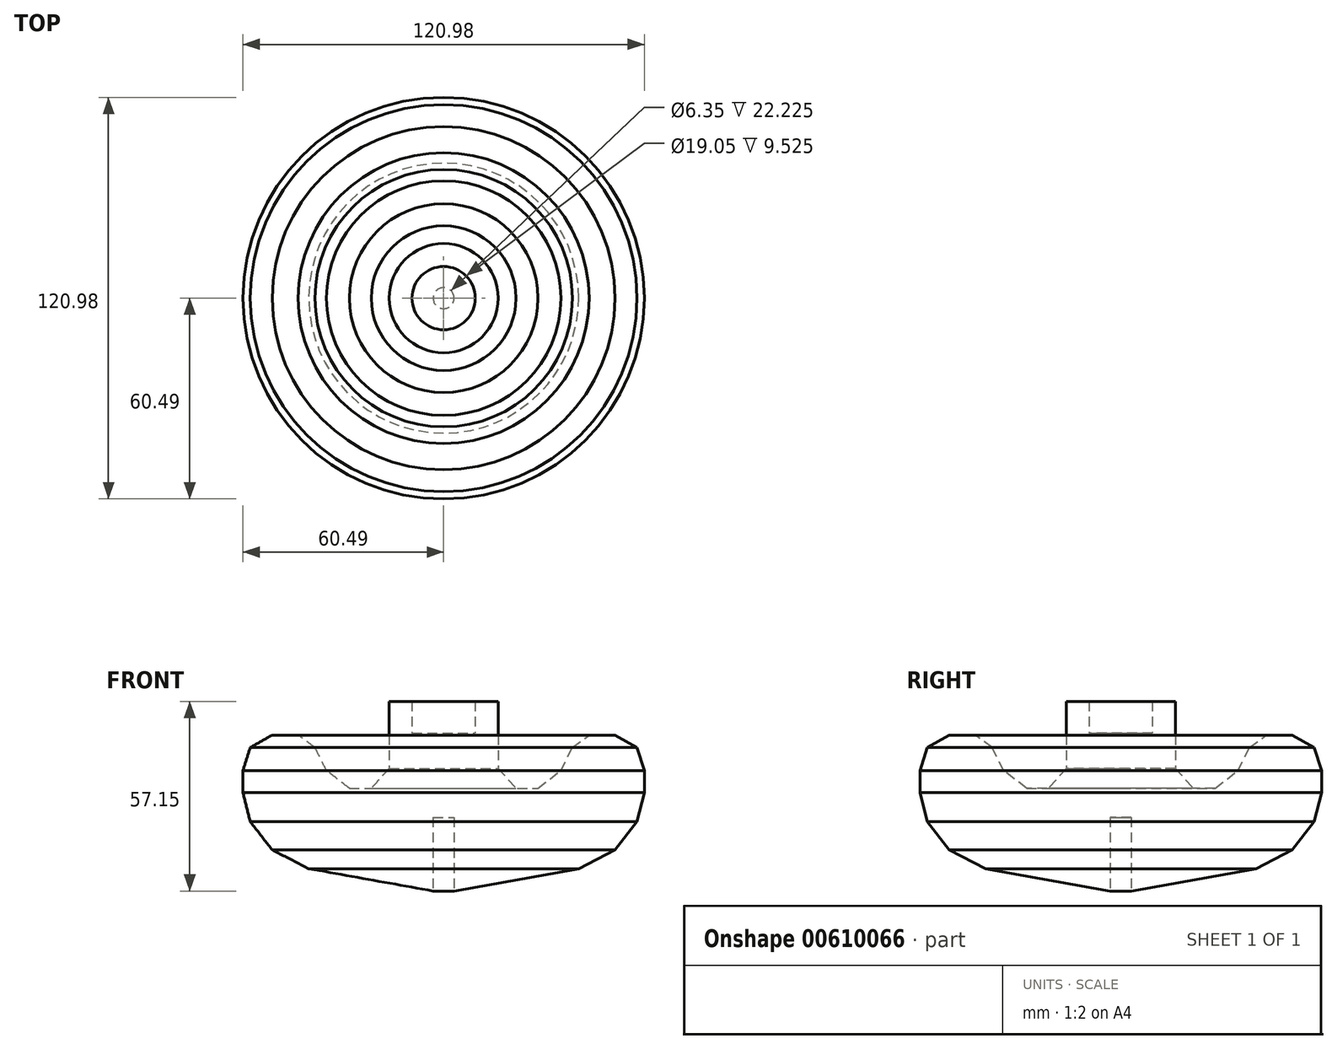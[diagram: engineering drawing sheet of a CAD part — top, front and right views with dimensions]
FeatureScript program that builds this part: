
annotation { "Feature Type Name" : "Feature", "Feature Type Description" : "" }
export const myFeature = defineFeature(function(context is Context, id is Id, definition is map)
    precondition{}
    {
        {
            var Q0;
            Q0=qCreatedBy(makeId("Front.planeOp"),FACE);
            var sketch = newSketch(context, id + "F0", { "sketchPlane" : qUnion([Q0])});
            skLineSegment(sketch, "E0", {"start": v(3.18, 0) * mm, "end": v(3.18, 22.23) * mm});
            skLineSegment(sketch, "E1", {"start": v(3.18, 22.22) * mm, "end": v(0, 22.22) * mm});
            skLineSegment(sketch, "E2", {"start": v(0, 22.22) * mm, "end": v(0, 47.62) * mm});
            skLineSegment(sketch, "E3", {"start": v(0, 47.62) * mm, "end": v(9.52, 47.62) * mm});
            skLineSegment(sketch, "E4", {"start": v(9.53, 47.62) * mm, "end": v(9.53, 57.15) * mm});
            skLineSegment(sketch, "E5", {"start": v(9.52, 57.15) * mm, "end": v(16.45, 57.15) * mm});
            skLineSegment(sketch, "E6", {"start": v(16.45, 57.15) * mm, "end": v(16.45, 47.62) * mm});
            skLineSegment(sketch, "E7", {"start": v(16.45, 47.62) * mm, "end": v(16.45, 36.94) * mm});
            skLineSegment(sketch, "E8", {"start": v(3.18, 0) * mm, "end": v(40.67, 6.74) * mm});
            skLineSegment(sketch, "E9", {"start": v(40.67, 6.74) * mm, "end": v(51.68, 12.4) * mm});
            skLineSegment(sketch, "E10", {"start": v(51.68, 12.4) * mm, "end": v(58.29, 20.9) * mm});
            skLineSegment(sketch, "E11", {"start": v(58.29, 20.9) * mm, "end": v(60.5, 29.7) * mm});
            skLineSegment(sketch, "E12", {"start": v(60.5, 29.7) * mm, "end": v(60.5, 36.3) * mm});
            skLineSegment(sketch, "E13", {"start": v(60.5, 36.3) * mm, "end": v(58.29, 43.23) * mm});
            skLineSegment(sketch, "E14", {"start": v(58.29, 43.23) * mm, "end": v(51.68, 47) * mm});
            skLineSegment(sketch, "E15", {"start": v(51.68, 47) * mm, "end": v(43.82, 47) * mm});
            skLineSegment(sketch, "E16", {"start": v(43.82, 47) * mm, "end": v(38.79, 43.23) * mm});
            skLineSegment(sketch, "E17", {"start": v(38.79, 43.23) * mm, "end": v(35.33, 36.3) * mm});
            skLineSegment(sketch, "E18", {"start": v(35.33, 36.3) * mm, "end": v(28.4, 30.96) * mm});
            skLineSegment(sketch, "E19", {"start": v(28.4, 30.96) * mm, "end": v(21.8, 30.96) * mm});
            skLineSegment(sketch, "E20", {"start": v(21.8, 30.96) * mm, "end": v(16.45, 36.94) * mm});
            skSolve(sketch);
        }
        {
            var Q0;
            Q0=makeQuery(id+"F0.imprint","IMPRINT",FACE,{"disambiguationData":[TD([[makeQuery(id+"F0.imprint","IMPRINT",EDGE,{"derivedFrom":sQuery(id+"F0.wireOp",EDGE,"E0")}),-1.0]])]});
            var Q1;
            Q1=sQuery(id+"F0.wireOp",EDGE,"E2");
            revolve(context, id + "F1", {"entities" : qUnion([Q0]), "axis" : qUnion([Q1]), "revolveType" : RevolveType.FULL});
        }
    });
